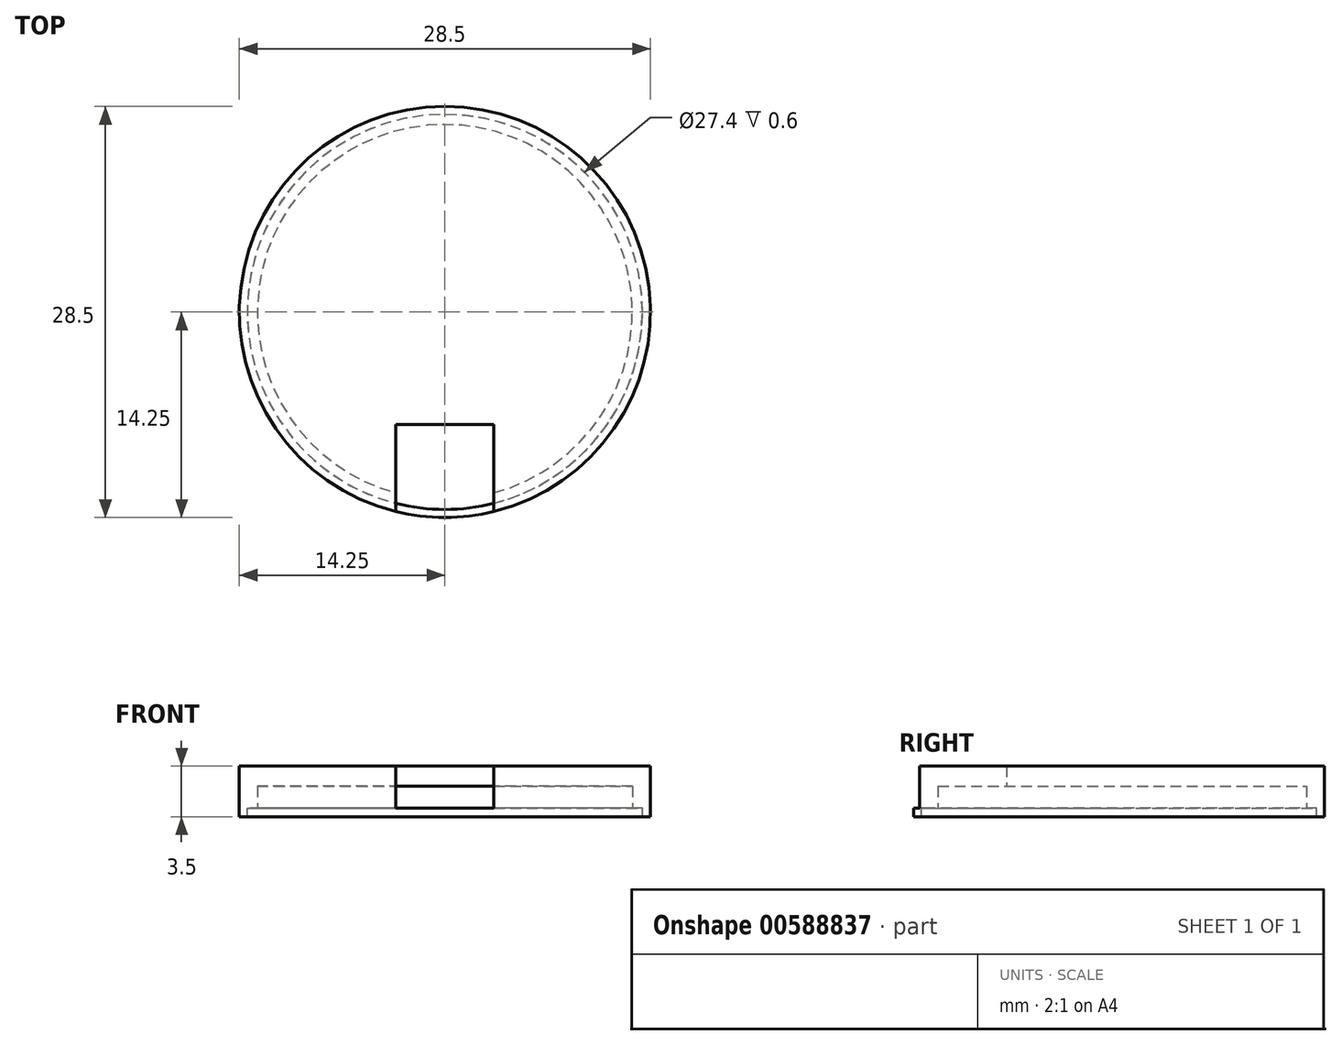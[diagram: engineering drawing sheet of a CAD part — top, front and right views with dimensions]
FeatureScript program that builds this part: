
annotation { "Feature Type Name" : "Feature", "Feature Type Description" : "" }
export const myFeature = defineFeature(function(context is Context, id is Id, definition is map)
    precondition{}
    {
        {
            var Q0;
            Q0=qCreatedBy(makeId("Top.planeOp"),FACE);
            var sketch = newSketch(context, id + "F0", { "sketchPlane" : qUnion([Q0])});
            skCircle(sketch, "E0", {"center": v(0, 0) * mm, "radius": 13.5 * mm});
            skLineSegment(sketch, "E1.bottom", {"start": v(3, -12.42) * mm, "end": v(-3, -12.42) * mm});
            skLineSegment(sketch, "E1.top", {"start": v(3, -8.17) * mm, "end": v(-3, -8.17) * mm});
            skLineSegment(sketch, "E1.left", {"start": v(3, -12.42) * mm, "end": v(3, -8.17) * mm});
            skLineSegment(sketch, "E1.right", {"start": v(-3, -12.42) * mm, "end": v(-3, -8.17) * mm});
            skPoint(sketch, "E1.middle", {"position": v(0, -10.3) * mm});
            skSolve(sketch);
        }
        {
            var Q0;
            Q0=qSketchRegion(id+"F0",true);
            var Q1;
            Q1=makeQuery(id+"F0.imprint","IMPRINT",FACE,{"disambiguationData":[TD([[makeQuery(id+"F0.imprint","IMPRINT",EDGE,{"derivedFrom":sQuery(id+"F0.wireOp",EDGE,"E1.bottom")}),-1.0]])]});
            extrude(context, id + "F1", {"entities" : qUnion([Q0, Q1]), "depth" : 1.2 * mm, "offsetDistance" : 25 * mm});
        }
        {
            var Q0;
            Q0=makeQuery(id+"F0.imprint","IMPRINT",FACE,{"disambiguationData":[TD([[makeQuery(id+"F0.imprint","IMPRINT",EDGE,{"derivedFrom":sQuery(id+"F0.wireOp",EDGE,"E1.bottom")}),-1.0]])]});
            extrude(context, id + "F2", {"entities" : qUnion([Q0]), "operationType" : NewBodyOperationType.ADD, "depth" : 4.2 * mm, "offsetDistance" : 25 * mm});
        }
        {
            var Q0;
            Q0=makeQuery(id+"F1.opExtrude","CAP_FACE",FACE,{"disambiguationData":[OSD([sQuery(id+"F0.wireOp",EDGE,"E0")])],"isStart":false});
            var sketch = newSketch(context, id + "F3", { "sketchPlane" : qUnion([Q0])});
            skCircle(sketch, "E2", {"center": v(0, 0) * mm, "radius": 14.25 * mm});
            skCircle(sketch, "E3", {"center": v(0, 0) * mm, "radius": 13.7 * mm});
            skLineSegment(sketch, "E4.bottom", {"start": v(3.4, -12.8) * mm, "end": v(-3.4, -12.8) * mm});
            skLineSegment(sketch, "E4.top", {"start": v(3.4, -7.8) * mm, "end": v(-3.4, -7.8) * mm});
            skLineSegment(sketch, "E4.left", {"start": v(3.4, -12.8) * mm, "end": v(3.4, -7.8) * mm});
            skLineSegment(sketch, "E4.right", {"start": v(-3.4, -12.8) * mm, "end": v(-3.4, -7.8) * mm});
            skPoint(sketch, "E4.middle", {"position": v(0, -10.3) * mm});
            skCircle(sketch, "E5", {"center": v(0, 0) * mm, "radius": 13 * mm});
            skSolve(sketch);
        }
        {
            var Q0;
            {var subQ0=sQuery(id+"F3.wireOp",EDGE,"E4.top");Q0=makeQuery(id+"F3.imprint","IMPRINT",FACE,{"disambiguationData":[TD([[makeQuery(id+"F3.imprint","IMPRINT",EDGE,{"derivedFrom":subQ0}),-1.0]])]});}
            var Q1;
            Q1=makeQuery(id+"F3.imprint","IMPRINT",FACE,{"disambiguationData":[TD([[makeQuery(id+"F3.imprint","IMPRINT",EDGE,{"derivedFrom":makeQuery(id+"F1.opExtrude","CAP_EDGE",EDGE,{"disambiguationData":[OSD([sQuery(id+"F0.wireOp",EDGE,"E0")])],"isStart":false})}),1.0]])]});
            var Q2;
            {var subQ0=sQuery(id+"F3.wireOp",EDGE,"E5");var subQ1=sQuery(id+"F3.wireOp",EDGE,"E4.bottom");var subQ2=makeQuery(id+"F3.imprint","INTERSECT",VERTEX,{"disambiguationData":[OD(0.0)],"derivedFrom":[subQ1,subQ0]});Q2=makeQuery(id+"F3.imprint","IMPRINT",FACE,{"disambiguationData":[TD([[makeQuery(id+"F3.imprint","IMPRINT",EDGE,{"disambiguationData":[TD([[subQ2,-1.0]])],"derivedFrom":subQ1}),1.0]])]});}
            var Q3;
            Q3=makeQuery(id+"F3.imprint","IMPRINT",FACE,{"disambiguationData":[TD([[makeQuery(id+"F3.imprint","IMPRINT",EDGE,{"derivedFrom":sQuery(id+"F3.wireOp",EDGE,"E3")}),1.0]])]});
            var Q4;
            Q4=makeQuery(id+"F3.imprint","IMPRINT",FACE,{"disambiguationData":[TD([[makeQuery(id+"F3.imprint","IMPRINT",EDGE,{"derivedFrom":sQuery(id+"F3.wireOp",EDGE,"E2")}),1.0]])]});
            extrude(context, id + "F4", {"entities" : qUnion([Q0, Q1, Q2, Q3, Q4]), "depth" : 2.9 * mm, "offsetDistance" : 25 * mm});
        }
        {
            var Q0;
            Q0=makeQuery(id+"F3.imprint","IMPRINT",FACE,{"disambiguationData":[TD([[makeQuery(id+"F3.imprint","IMPRINT",EDGE,{"derivedFrom":sQuery(id+"F3.wireOp",EDGE,"E2")}),1.0]])]});
            extrude(context, id + "F5", {"entities" : qUnion([Q0]), "operationType" : NewBodyOperationType.ADD, "oppositeDirection" : true, "depth" : 0.6 * mm, "offsetDistance" : 25 * mm});
        }
        {
            var Q0;
            {var subQ0=sQuery(id+"F3.wireOp",EDGE,"E4.top");Q0=makeQuery(id+"F3.imprint","IMPRINT",FACE,{"disambiguationData":[TD([[makeQuery(id+"F3.imprint","IMPRINT",EDGE,{"derivedFrom":subQ0}),-1.0]])]});}
            var Q1;
            {var subQ1=sQuery(id+"F3.wireOp",EDGE,"E4.top");Q1=makeQuery(id+"F3.imprint","IMPRINT",FACE,{"disambiguationData":[TD([[makeQuery(id+"F3.imprint","IMPRINT",EDGE,{"derivedFrom":subQ1}),1.0]])]});}
            var Q2;
            {var subQ0=sQuery(id+"F3.wireOp",EDGE,"E5");var subQ1=sQuery(id+"F3.wireOp",EDGE,"E4.bottom");var subQ2=makeQuery(id+"F3.imprint","INTERSECT",VERTEX,{"disambiguationData":[OD(0.0)],"derivedFrom":[subQ1,subQ0]});Q2=makeQuery(id+"F3.imprint","IMPRINT",FACE,{"disambiguationData":[TD([[makeQuery(id+"F3.imprint","IMPRINT",EDGE,{"disambiguationData":[TD([[subQ2,-1.0]])],"derivedFrom":subQ1}),1.0]])]});}
            var Q3;
            {var subQ0=makeQuery(id+"F1.opExtrude","CAP_FACE",FACE,{"disambiguationData":[OSD([sQuery(id+"F0.wireOp",EDGE,"E0")])],"isStart":false});Q3=makeQuery(id+"F3.imprint","IMPRINT",FACE,{"disambiguationData":[TD([[makeQuery(id+"F3.imprint","IMPRINT",EDGE,{"derivedFrom":makeQuery(id+"F2.boolean.opBoolean","INTERSECT",EDGE,{"derivedFrom":[subQ0,makeQuery(id+"F2.opExtrude","SWEPT_FACE",FACE,{"disambiguationData":[OSD([sQuery(id+"F0.wireOp",EDGE,"E1.bottom")])]})]})}),1.0]])]});}
            var Q4;
            Q4=sQuery(id+"F3.wireOp",EDGE,"E5");
            extrude(context, id + "F6", {"entities" : qUnion([Q0, Q1, Q2, Q3]), "operationType" : NewBodyOperationType.REMOVE, "surfaceEntities" : qUnion([Q4]), "depth" : 1.5 * mm, "offsetDistance" : 25 * mm});
        }
        {
            var Q0;
            Q0=makeQuery(id+"F2.opExtrude","SWEPT_FACE",FACE,{"disambiguationData":[OSD([sQuery(id+"F0.wireOp",EDGE,"E1.bottom")])]});
            var sketch = newSketch(context, id + "F7", { "sketchPlane" : qUnion([Q0])});
            skLineSegment(sketch, "E6.bottom", {"start": v(-3.4, 4.2) * mm, "end": v(3.4, 4.2) * mm});
            skLineSegment(sketch, "E6.top", {"start": v(-3.4, 1.2) * mm, "end": v(3.4, 1.2) * mm});
            skLineSegment(sketch, "E6.left", {"start": v(-3.4, 4.2) * mm, "end": v(-3.4, 1.2) * mm});
            skLineSegment(sketch, "E6.right", {"start": v(3.4, 4.2) * mm, "end": v(3.4, 1.2) * mm});
            skSolve(sketch);
        }
        {
            var Q0;
            Q0=qSketchRegion(id+"F7",true);
            extrude(context, id + "F8", {"entities" : qUnion([Q0]), "operationType" : NewBodyOperationType.REMOVE, "depth" : 8 * mm, "offsetDistance" : 25 * mm});
        }
        {
            var Q0;
            Q0=makeQuery(id+"F1.opExtrude","SWEPT_BODY",BODY,{"disambiguationData":[OSD([sQuery(id+"F0.wireOp",EDGE,"E0")])]});
            deleteBodies(context, id + "F9", {"entities" : qUnion([Q0])});
        }
    });
